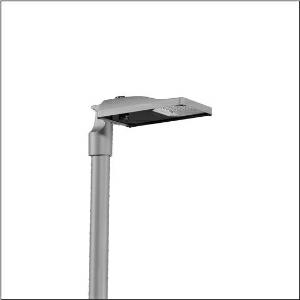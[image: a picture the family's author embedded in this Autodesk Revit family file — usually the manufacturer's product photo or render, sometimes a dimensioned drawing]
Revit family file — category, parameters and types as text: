
# Revit family: streetlight_sl_31_micro___st0_5a_5xh5b31t08ca_3c37
name_source: partatom
category: Lighting Fixtures
units: mm (PartAtom-declared; Revit-internal decimal feet)

## family parameters
Cut with Voids When Loaded = No
Host = Face
Light Source = No
Part Type = Normal
Room Calculation Point = No
Round Connector Dimension = Use Diameter
Shared = No

## types (1)
- --- (1 x LED, 1440 lm, 10.2 W, 3000K)
    Apparent Load = 10 VA
    CIE Flux Codes = 41 75 97 100 100
    Color Rendering = 70
    Color Temperature = 3000K
    Default Elevation = 1800 mm
    Description = Streetlight SL 31 micro D4i, Desk-Remote mast luminaire for post-top, side-entry; light control with lens of PMMA; light distribution: ST0.5a, direct asymmetric distribution, for standard-compliant lighting for roads and squares; LED: luminous flux: 1.440lm, light colour: 730, colour temperature: 3000K; luminous efficacy: 141,2lm/W; control: pre-setting: logarithmic dimming characteristic, flexible luminous flux parameterisation, time-dependent luminous flux control, constant luminous flux control, power reduction, intelligent temperature release in ECG and LED module, overheat protection; luminaire housing, of diecast aluminium, Siteco® metallic grey (DB 702S), corrosivity category C5 high according to DIN EN ISO 12944; cover of toughened safety glass, transparent, opened without tools; mast flange of diecast aluminium, Siteco® metallic grey (DB 702S), spigot size: 76/60mm, mast flange included unmounted; with cable H07RN-F 2x 1.5mm², cable length: 5,5m, connection cable pre-assembled; mains connection: 220..240V, AC, 50/60Hz; power consumption (at start of service life): 10,2W / (at end of service life): 10,5W / (with reduced operation 50%): 5,3W; protection rating (complete): IP66; insulation class (complete): insulation class II (safety insulation); impact resistance: IK09; certification: CE, ENEC, ENEC+, VDE, UKCA, ZD4i; permissible operating ambient temperature for outdoor applications: -40..+50°C; packaging unit: 1 piece

Light Distribution: ST0.5a
    Height = 76 mm
    Lamp = 1 x LED
    Lamp Light Flux = 1440 lm
    Lamp Power = 10.2 W
    Lamp count = 1
    Length = 467 mm
    Luminous efficacy = 141 lm/W
    Manufacturer = Siteco
    ModVariant = No
    Model = 5XH5B31T08CA
    Number of Poles = 1
    OnlyDefault = Yes
    Power Factor = 1
    Product Name = Streetlight SL 31 micro | ST0.5a
    Product group = mast luminaire | pylon top
    ProductGroupID = 6100
    Protection Class = Protection class II
    Protection Degree = IP 66
    RLX_Detail_Level = 1
    RLX_Emergency_Light_Flux = 0 lm
    RLX_Emergency_Type = 0
    RLX_Emergency_Type_DB = No
    RlxData = <blob elided: 55233 chars, md5=d724b971>
    Socket = socket
    Standby Power = 0 W
    System Light Flux = 1440 lm
    System Power = 10 W
    Type Comments = factory setting: luminous flux: 100 % | dim-lin: 254 | 386 mA
    Type Image = l_1300315.jpg
    URL = http://relux.com
    VarID = @adj_048418
    Voltage = 0 V
    Weight = 0.00 kg
    Width = 265 mm

## geometry (parser evidence)
native form markers: Blend x4, Sweep x9
no freeform markers — native parametric forms only
